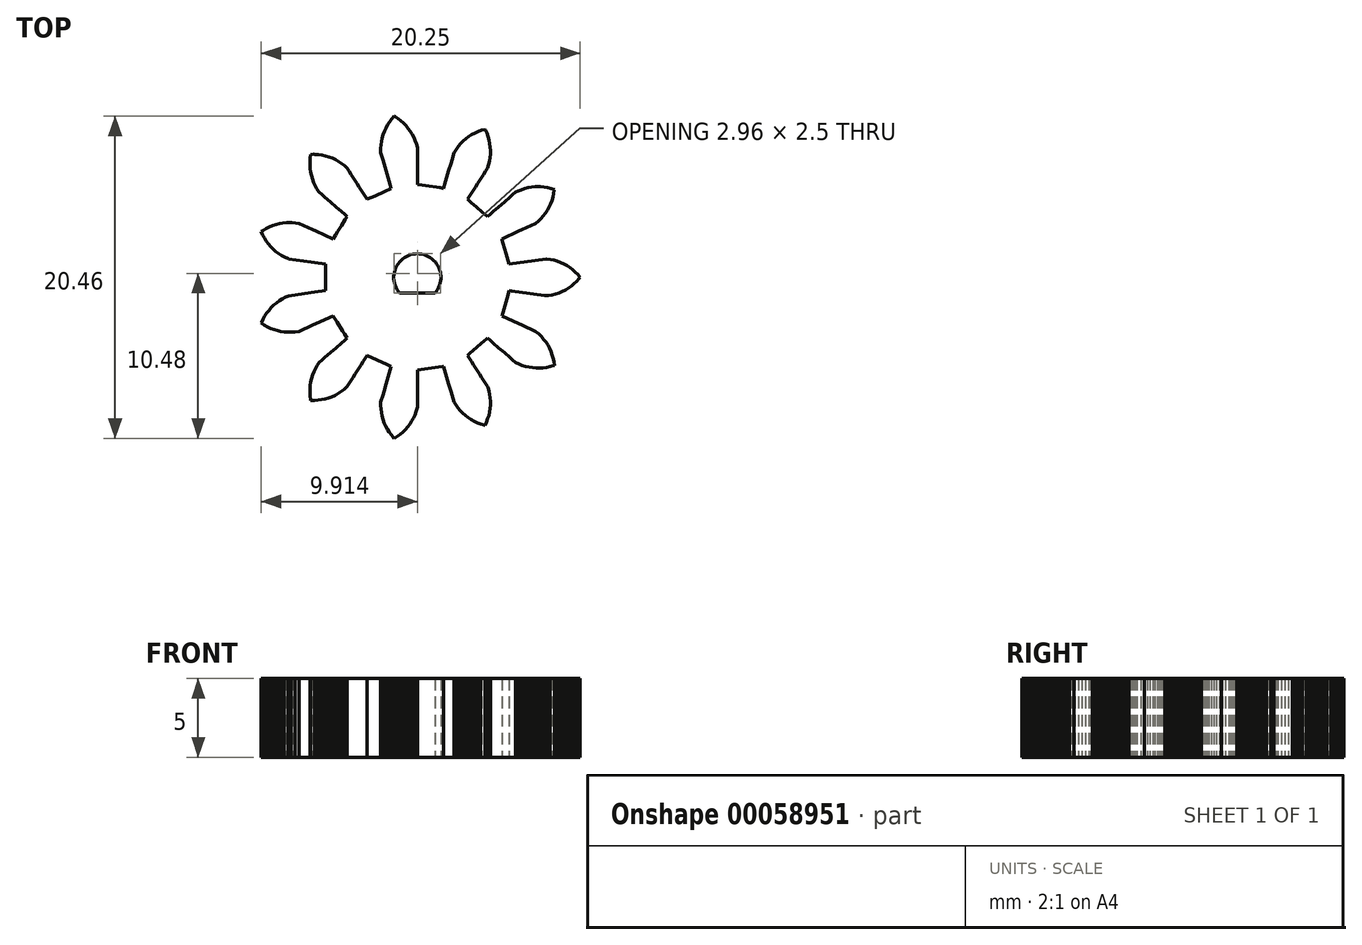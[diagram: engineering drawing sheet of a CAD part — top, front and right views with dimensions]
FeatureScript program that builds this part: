
annotation { "Feature Type Name" : "Feature", "Feature Type Description" : "" }
export const myFeature = defineFeature(function(context is Context, id is Id, definition is map)
    precondition{}
    {
        {
            var Q0;
            Q0=qCreatedBy(makeId("Top.planeOp"),FACE);
            var sketch = newSketch(context, id + "F0", { "sketchPlane" : qUnion([Q0])});
            skLineSegment(sketch, "E0", {"start": v(4.2, -0.84) * mm, "end": v(4.36, -0.86) * mm});
            skLineSegment(sketch, "E1", {"start": v(4.36, -0.86) * mm, "end": v(4.6, -0.9) * mm});
            skLineSegment(sketch, "E2", {"start": v(4.6, -0.9) * mm, "end": v(4.83, -0.93) * mm});
            skLineSegment(sketch, "E3", {"start": v(4.83, -0.93) * mm, "end": v(5.06, -0.96) * mm});
            skLineSegment(sketch, "E4", {"start": v(5.06, -0.96) * mm, "end": v(5.3, -1) * mm});
            skLineSegment(sketch, "E5", {"start": v(5.3, -1) * mm, "end": v(5.53, -1.03) * mm});
            skLineSegment(sketch, "E6", {"start": v(5.53, -1.03) * mm, "end": v(5.76, -1.06) * mm});
            skLineSegment(sketch, "E7", {"start": v(5.76, -1.06) * mm, "end": v(6, -1.1) * mm});
            skLineSegment(sketch, "E8", {"start": v(6, -1.1) * mm, "end": v(6.23, -1.13) * mm});
            skLineSegment(sketch, "E9", {"start": v(6.23, -1.13) * mm, "end": v(6.46, -1.16) * mm});
            skLineSegment(sketch, "E10", {"start": v(6.46, -1.16) * mm, "end": v(6.7, -1.16) * mm});
            skLineSegment(sketch, "E11", {"start": v(6.7, -1.16) * mm, "end": v(6.93, -1.11) * mm});
            skLineSegment(sketch, "E12", {"start": v(6.93, -1.11) * mm, "end": v(7.16, -1.06) * mm});
            skLineSegment(sketch, "E13", {"start": v(7.16, -1.06) * mm, "end": v(7.36, -0.99) * mm});
            skLineSegment(sketch, "E14", {"start": v(7.36, -0.99) * mm, "end": v(7.57, -0.9) * mm});
            skLineSegment(sketch, "E15", {"start": v(7.57, -0.9) * mm, "end": v(7.78, -0.8) * mm});
            skLineSegment(sketch, "E16", {"start": v(7.78, -0.8) * mm, "end": v(7.97, -0.68) * mm});
            skLineSegment(sketch, "E17", {"start": v(7.97, -0.68) * mm, "end": v(8.15, -0.55) * mm});
            skLineSegment(sketch, "E18", {"start": v(8.15, -0.55) * mm, "end": v(8.33, -0.4) * mm});
            skLineSegment(sketch, "E19", {"start": v(8.33, -0.4) * mm, "end": v(8.49, -0.26) * mm});
            skLineSegment(sketch, "E20", {"start": v(8.49, -0.26) * mm, "end": v(8.64, -0.08) * mm});
            skLineSegment(sketch, "E21", {"start": v(8.64, -0.08) * mm, "end": v(8.7, 0) * mm});
            skLineSegment(sketch, "E22", {"start": v(8.7, 0) * mm, "end": v(8.56, 0.17) * mm});
            skLineSegment(sketch, "E23", {"start": v(8.56, 0.17) * mm, "end": v(8.4, 0.34) * mm});
            skLineSegment(sketch, "E24", {"start": v(8.4, 0.34) * mm, "end": v(8.24, 0.48) * mm});
            skLineSegment(sketch, "E25", {"start": v(8.24, 0.48) * mm, "end": v(8.06, 0.62) * mm});
            skLineSegment(sketch, "E26", {"start": v(8.06, 0.62) * mm, "end": v(7.86, 0.75) * mm});
            skLineSegment(sketch, "E27", {"start": v(7.86, 0.75) * mm, "end": v(7.67, 0.85) * mm});
            skLineSegment(sketch, "E28", {"start": v(7.67, 0.85) * mm, "end": v(7.46, 0.95) * mm});
            skLineSegment(sketch, "E29", {"start": v(7.46, 0.95) * mm, "end": v(7.25, 1.03) * mm});
            skLineSegment(sketch, "E30", {"start": v(7.25, 1.03) * mm, "end": v(7.04, 1.1) * mm});
            skLineSegment(sketch, "E31", {"start": v(7.04, 1.1) * mm, "end": v(6.82, 1.14) * mm});
            skLineSegment(sketch, "E32", {"start": v(6.82, 1.14) * mm, "end": v(6.59, 1.17) * mm});
            skLineSegment(sketch, "E33", {"start": v(6.59, 1.17) * mm, "end": v(6.54, 1.17) * mm});
            skLineSegment(sketch, "E34", {"start": v(6.54, 1.17) * mm, "end": v(6.3, 1.14) * mm});
            skLineSegment(sketch, "E35", {"start": v(6.3, 1.14) * mm, "end": v(6.07, 1.1) * mm});
            skLineSegment(sketch, "E36", {"start": v(6.07, 1.1) * mm, "end": v(5.84, 1.07) * mm});
            skLineSegment(sketch, "E37", {"start": v(5.84, 1.07) * mm, "end": v(5.6, 1.04) * mm});
            skLineSegment(sketch, "E38", {"start": v(5.6, 1.04) * mm, "end": v(5.37, 1) * mm});
            skLineSegment(sketch, "E39", {"start": v(5.37, 1) * mm, "end": v(5.14, 0.97) * mm});
            skLineSegment(sketch, "E40", {"start": v(5.14, 0.97) * mm, "end": v(4.9, 0.94) * mm});
            skLineSegment(sketch, "E41", {"start": v(4.9, 0.94) * mm, "end": v(4.67, 0.9) * mm});
            skLineSegment(sketch, "E42", {"start": v(4.67, 0.9) * mm, "end": v(4.44, 0.87) * mm});
            skLineSegment(sketch, "E43", {"start": v(4.44, 0.87) * mm, "end": v(4.2, 0.84) * mm});
            skLineSegment(sketch, "E44", {"start": v(4.2, 0.84) * mm, "end": v(4.14, 1.06) * mm});
            skLineSegment(sketch, "E45", {"start": v(4.14, 1.06) * mm, "end": v(4.08, 1.28) * mm});
            skLineSegment(sketch, "E46", {"start": v(4.08, 1.28) * mm, "end": v(4.01, 1.5) * mm});
            skLineSegment(sketch, "E47", {"start": v(4.01, 1.5) * mm, "end": v(3.95, 1.72) * mm});
            skLineSegment(sketch, "E48", {"start": v(3.95, 1.72) * mm, "end": v(3.88, 1.94) * mm});
            skLineSegment(sketch, "E49", {"start": v(3.88, 1.94) * mm, "end": v(3.82, 2.16) * mm});
            skLineSegment(sketch, "E50", {"start": v(3.82, 2.16) * mm, "end": v(3.76, 2.38) * mm});
            skLineSegment(sketch, "E51", {"start": v(3.76, 2.38) * mm, "end": v(3.74, 2.45) * mm});
            skLineSegment(sketch, "E52", {"start": v(3.74, 2.45) * mm, "end": v(3.95, 2.55) * mm});
            skLineSegment(sketch, "E53", {"start": v(3.95, 2.55) * mm, "end": v(4.16, 2.64) * mm});
            skLineSegment(sketch, "E54", {"start": v(4.16, 2.64) * mm, "end": v(4.38, 2.74) * mm});
            skLineSegment(sketch, "E55", {"start": v(4.38, 2.74) * mm, "end": v(4.6, 2.84) * mm});
            skLineSegment(sketch, "E56", {"start": v(4.6, 2.84) * mm, "end": v(4.8, 2.94) * mm});
            skLineSegment(sketch, "E57", {"start": v(4.8, 2.94) * mm, "end": v(5.02, 3.04) * mm});
            skLineSegment(sketch, "E58", {"start": v(5.02, 3.04) * mm, "end": v(5.24, 3.13) * mm});
            skLineSegment(sketch, "E59", {"start": v(5.24, 3.13) * mm, "end": v(5.45, 3.23) * mm});
            skLineSegment(sketch, "E60", {"start": v(5.45, 3.23) * mm, "end": v(5.66, 3.33) * mm});
            skLineSegment(sketch, "E61", {"start": v(5.66, 3.33) * mm, "end": v(5.88, 3.43) * mm});
            skLineSegment(sketch, "E62", {"start": v(5.88, 3.43) * mm, "end": v(6.05, 3.57) * mm});
            skLineSegment(sketch, "E63", {"start": v(6.05, 3.57) * mm, "end": v(6.22, 3.73) * mm});
            skLineSegment(sketch, "E64", {"start": v(6.22, 3.73) * mm, "end": v(6.37, 3.9) * mm});
            skLineSegment(sketch, "E65", {"start": v(6.37, 3.9) * mm, "end": v(6.5, 4.08) * mm});
            skLineSegment(sketch, "E66", {"start": v(6.5, 4.08) * mm, "end": v(6.63, 4.27) * mm});
            skLineSegment(sketch, "E67", {"start": v(6.63, 4.27) * mm, "end": v(6.74, 4.46) * mm});
            skLineSegment(sketch, "E68", {"start": v(6.74, 4.46) * mm, "end": v(6.84, 4.67) * mm});
            skLineSegment(sketch, "E69", {"start": v(6.84, 4.67) * mm, "end": v(6.92, 4.88) * mm});
            skLineSegment(sketch, "E70", {"start": v(6.92, 4.88) * mm, "end": v(6.98, 5.09) * mm});
            skLineSegment(sketch, "E71", {"start": v(6.98, 5.09) * mm, "end": v(7.03, 5.31) * mm});
            skLineSegment(sketch, "E72", {"start": v(7.03, 5.31) * mm, "end": v(7.06, 5.54) * mm});
            skLineSegment(sketch, "E73", {"start": v(7.06, 5.54) * mm, "end": v(7.07, 5.59) * mm});
            skLineSegment(sketch, "E74", {"start": v(7.07, 5.59) * mm, "end": v(6.85, 5.65) * mm});
            skLineSegment(sketch, "E75", {"start": v(6.85, 5.65) * mm, "end": v(6.63, 5.7) * mm});
            skLineSegment(sketch, "E76", {"start": v(6.63, 5.7) * mm, "end": v(6.41, 5.74) * mm});
            skLineSegment(sketch, "E77", {"start": v(6.41, 5.74) * mm, "end": v(6.18, 5.76) * mm});
            skLineSegment(sketch, "E78", {"start": v(6.18, 5.76) * mm, "end": v(6.07, 5.76) * mm});
            skLineSegment(sketch, "E79", {"start": v(6.07, 5.76) * mm, "end": v(5.84, 5.75) * mm});
            skLineSegment(sketch, "E80", {"start": v(5.84, 5.75) * mm, "end": v(5.62, 5.73) * mm});
            skLineSegment(sketch, "E81", {"start": v(5.62, 5.73) * mm, "end": v(5.4, 5.7) * mm});
            skLineSegment(sketch, "E82", {"start": v(5.4, 5.7) * mm, "end": v(5.18, 5.63) * mm});
            skLineSegment(sketch, "E83", {"start": v(5.18, 5.63) * mm, "end": v(4.96, 5.56) * mm});
            skLineSegment(sketch, "E84", {"start": v(4.96, 5.56) * mm, "end": v(4.76, 5.48) * mm});
            skLineSegment(sketch, "E85", {"start": v(4.76, 5.48) * mm, "end": v(4.6, 5.4) * mm});
            skLineSegment(sketch, "E86", {"start": v(4.6, 5.4) * mm, "end": v(4.43, 5.25) * mm});
            skLineSegment(sketch, "E87", {"start": v(4.43, 5.25) * mm, "end": v(4.25, 5.1) * mm});
            skLineSegment(sketch, "E88", {"start": v(4.25, 5.1) * mm, "end": v(4.07, 4.94) * mm});
            skLineSegment(sketch, "E89", {"start": v(4.07, 4.94) * mm, "end": v(3.9, 4.79) * mm});
            skLineSegment(sketch, "E90", {"start": v(3.9, 4.79) * mm, "end": v(3.72, 4.63) * mm});
            skLineSegment(sketch, "E91", {"start": v(3.72, 4.63) * mm, "end": v(3.54, 4.48) * mm});
            skLineSegment(sketch, "E92", {"start": v(3.54, 4.48) * mm, "end": v(3.36, 4.32) * mm});
            skLineSegment(sketch, "E93", {"start": v(3.36, 4.32) * mm, "end": v(3.18, 4.17) * mm});
            skLineSegment(sketch, "E94", {"start": v(3.18, 4.17) * mm, "end": v(3, 4.01) * mm});
            skLineSegment(sketch, "E95", {"start": v(3, 4.01) * mm, "end": v(2.83, 3.86) * mm});
            skLineSegment(sketch, "E96", {"start": v(2.83, 3.86) * mm, "end": v(2.65, 4) * mm});
            skLineSegment(sketch, "E97", {"start": v(2.65, 4) * mm, "end": v(2.48, 4.16) * mm});
            skLineSegment(sketch, "E98", {"start": v(2.48, 4.16) * mm, "end": v(2.3, 4.31) * mm});
            skLineSegment(sketch, "E99", {"start": v(2.3, 4.31) * mm, "end": v(2.13, 4.46) * mm});
            skLineSegment(sketch, "E100", {"start": v(2.13, 4.46) * mm, "end": v(1.96, 4.61) * mm});
            skLineSegment(sketch, "E101", {"start": v(1.96, 4.61) * mm, "end": v(1.79, 4.76) * mm});
            skLineSegment(sketch, "E102", {"start": v(1.79, 4.76) * mm, "end": v(1.62, 4.91) * mm});
            skLineSegment(sketch, "E103", {"start": v(1.62, 4.91) * mm, "end": v(1.56, 4.96) * mm});
            skLineSegment(sketch, "E104", {"start": v(1.56, 4.96) * mm, "end": v(1.69, 5.16) * mm});
            skLineSegment(sketch, "E105", {"start": v(1.69, 5.16) * mm, "end": v(1.82, 5.35) * mm});
            skLineSegment(sketch, "E106", {"start": v(1.82, 5.35) * mm, "end": v(1.94, 5.55) * mm});
            skLineSegment(sketch, "E107", {"start": v(1.94, 5.55) * mm, "end": v(2.07, 5.75) * mm});
            skLineSegment(sketch, "E108", {"start": v(2.07, 5.75) * mm, "end": v(2.2, 5.95) * mm});
            skLineSegment(sketch, "E109", {"start": v(2.2, 5.95) * mm, "end": v(2.32, 6.15) * mm});
            skLineSegment(sketch, "E110", {"start": v(2.32, 6.15) * mm, "end": v(2.45, 6.35) * mm});
            skLineSegment(sketch, "E111", {"start": v(2.45, 6.35) * mm, "end": v(2.58, 6.54) * mm});
            skLineSegment(sketch, "E112", {"start": v(2.58, 6.54) * mm, "end": v(2.7, 6.74) * mm});
            skLineSegment(sketch, "E113", {"start": v(2.7, 6.74) * mm, "end": v(2.83, 6.94) * mm});
            skLineSegment(sketch, "E114", {"start": v(2.83, 6.94) * mm, "end": v(2.9, 7.16) * mm});
            skLineSegment(sketch, "E115", {"start": v(2.9, 7.16) * mm, "end": v(2.95, 7.38) * mm});
            skLineSegment(sketch, "E116", {"start": v(2.95, 7.38) * mm, "end": v(3, 7.6) * mm});
            skLineSegment(sketch, "E117", {"start": v(3, 7.6) * mm, "end": v(3.01, 7.83) * mm});
            skLineSegment(sketch, "E118", {"start": v(3.01, 7.83) * mm, "end": v(3.01, 8.06) * mm});
            skLineSegment(sketch, "E119", {"start": v(3.01, 8.06) * mm, "end": v(3, 8.27) * mm});
            skLineSegment(sketch, "E120", {"start": v(3, 8.27) * mm, "end": v(2.97, 8.5) * mm});
            skLineSegment(sketch, "E121", {"start": v(2.97, 8.5) * mm, "end": v(2.92, 8.72) * mm});
            skLineSegment(sketch, "E122", {"start": v(2.92, 8.72) * mm, "end": v(2.86, 8.93) * mm});
            skLineSegment(sketch, "E123", {"start": v(2.86, 8.93) * mm, "end": v(2.78, 9.15) * mm});
            skLineSegment(sketch, "E124", {"start": v(2.78, 9.15) * mm, "end": v(2.69, 9.36) * mm});
            skLineSegment(sketch, "E125", {"start": v(2.69, 9.36) * mm, "end": v(2.67, 9.4) * mm});
            skLineSegment(sketch, "E126", {"start": v(2.67, 9.4) * mm, "end": v(2.45, 9.34) * mm});
            skLineSegment(sketch, "E127", {"start": v(2.45, 9.34) * mm, "end": v(2.23, 9.26) * mm});
            skLineSegment(sketch, "E128", {"start": v(2.23, 9.26) * mm, "end": v(2.03, 9.17) * mm});
            skLineSegment(sketch, "E129", {"start": v(2.03, 9.17) * mm, "end": v(1.83, 9.06) * mm});
            skLineSegment(sketch, "E130", {"start": v(1.83, 9.06) * mm, "end": v(1.64, 8.94) * mm});
            skLineSegment(sketch, "E131", {"start": v(1.64, 8.94) * mm, "end": v(1.46, 8.81) * mm});
            skLineSegment(sketch, "E132", {"start": v(1.46, 8.81) * mm, "end": v(1.29, 8.66) * mm});
            skLineSegment(sketch, "E133", {"start": v(1.29, 8.66) * mm, "end": v(1.13, 8.5) * mm});
            skLineSegment(sketch, "E134", {"start": v(1.13, 8.5) * mm, "end": v(0.98, 8.34) * mm});
            skLineSegment(sketch, "E135", {"start": v(0.98, 8.34) * mm, "end": v(0.85, 8.15) * mm});
            skLineSegment(sketch, "E136", {"start": v(0.85, 8.15) * mm, "end": v(0.72, 7.96) * mm});
            skLineSegment(sketch, "E137", {"start": v(0.72, 7.96) * mm, "end": v(0.7, 7.92) * mm});
            skLineSegment(sketch, "E138", {"start": v(0.7, 7.92) * mm, "end": v(0.63, 7.69) * mm});
            skLineSegment(sketch, "E139", {"start": v(0.63, 7.69) * mm, "end": v(0.57, 7.46) * mm});
            skLineSegment(sketch, "E140", {"start": v(0.57, 7.46) * mm, "end": v(0.5, 7.24) * mm});
            skLineSegment(sketch, "E141", {"start": v(0.5, 7.24) * mm, "end": v(0.43, 7.01) * mm});
            skLineSegment(sketch, "E142", {"start": v(0.43, 7.01) * mm, "end": v(0.37, 6.79) * mm});
            skLineSegment(sketch, "E143", {"start": v(0.37, 6.79) * mm, "end": v(0.3, 6.56) * mm});
            skLineSegment(sketch, "E144", {"start": v(0.3, 6.56) * mm, "end": v(0.23, 6.33) * mm});
            skLineSegment(sketch, "E145", {"start": v(0.23, 6.33) * mm, "end": v(0.17, 6.1) * mm});
            skLineSegment(sketch, "E146", {"start": v(0.17, 6.1) * mm, "end": v(0.1, 5.88) * mm});
            skLineSegment(sketch, "E147", {"start": v(0.1, 5.88) * mm, "end": v(0.03, 5.66) * mm});
            skLineSegment(sketch, "E148", {"start": v(0.03, 5.66) * mm, "end": v(-0.2, 5.69) * mm});
            skLineSegment(sketch, "E149", {"start": v(-0.2, 5.69) * mm, "end": v(-0.42, 5.72) * mm});
            skLineSegment(sketch, "E150", {"start": v(-0.42, 5.72) * mm, "end": v(-0.65, 5.75) * mm});
            skLineSegment(sketch, "E151", {"start": v(-0.65, 5.75) * mm, "end": v(-0.87, 5.79) * mm});
            skLineSegment(sketch, "E152", {"start": v(-0.87, 5.79) * mm, "end": v(-1.1, 5.82) * mm});
            skLineSegment(sketch, "E153", {"start": v(-1.1, 5.82) * mm, "end": v(-1.33, 5.85) * mm});
            skLineSegment(sketch, "E154", {"start": v(-1.33, 5.85) * mm, "end": v(-1.55, 5.88) * mm});
            skLineSegment(sketch, "E155", {"start": v(-1.55, 5.88) * mm, "end": v(-1.63, 5.9) * mm});
            skLineSegment(sketch, "E156", {"start": v(-1.63, 5.9) * mm, "end": v(-1.63, 6.13) * mm});
            skLineSegment(sketch, "E157", {"start": v(-1.63, 6.13) * mm, "end": v(-1.63, 6.37) * mm});
            skLineSegment(sketch, "E158", {"start": v(-1.63, 6.37) * mm, "end": v(-1.63, 6.6) * mm});
            skLineSegment(sketch, "E159", {"start": v(-1.63, 6.6) * mm, "end": v(-1.63, 6.84) * mm});
            skLineSegment(sketch, "E160", {"start": v(-1.63, 6.84) * mm, "end": v(-1.63, 7.07) * mm});
            skLineSegment(sketch, "E161", {"start": v(-1.63, 7.07) * mm, "end": v(-1.63, 7.3) * mm});
            skLineSegment(sketch, "E162", {"start": v(-1.63, 7.3) * mm, "end": v(-1.63, 7.54) * mm});
            skLineSegment(sketch, "E163", {"start": v(-1.63, 7.54) * mm, "end": v(-1.63, 7.78) * mm});
            skLineSegment(sketch, "E164", {"start": v(-1.63, 7.78) * mm, "end": v(-1.63, 8.01) * mm});
            skLineSegment(sketch, "E165", {"start": v(-1.63, 8.01) * mm, "end": v(-1.63, 8.25) * mm});
            skLineSegment(sketch, "E166", {"start": v(-1.63, 8.25) * mm, "end": v(-1.69, 8.47) * mm});
            skLineSegment(sketch, "E167", {"start": v(-1.69, 8.47) * mm, "end": v(-1.76, 8.69) * mm});
            skLineSegment(sketch, "E168", {"start": v(-1.76, 8.69) * mm, "end": v(-1.85, 8.89) * mm});
            skLineSegment(sketch, "E169", {"start": v(-1.85, 8.89) * mm, "end": v(-1.96, 9.1) * mm});
            skLineSegment(sketch, "E170", {"start": v(-1.96, 9.1) * mm, "end": v(-2.08, 9.28) * mm});
            skLineSegment(sketch, "E171", {"start": v(-2.08, 9.28) * mm, "end": v(-2.2, 9.46) * mm});
            skLineSegment(sketch, "E172", {"start": v(-2.2, 9.46) * mm, "end": v(-2.35, 9.64) * mm});
            skLineSegment(sketch, "E173", {"start": v(-2.35, 9.64) * mm, "end": v(-2.52, 9.8) * mm});
            skLineSegment(sketch, "E174", {"start": v(-2.52, 9.8) * mm, "end": v(-2.68, 9.94) * mm});
            skLineSegment(sketch, "E175", {"start": v(-2.68, 9.94) * mm, "end": v(-2.86, 10.08) * mm});
            skLineSegment(sketch, "E176", {"start": v(-2.86, 10.08) * mm, "end": v(-3.06, 10.2) * mm});
            skLineSegment(sketch, "E177", {"start": v(-3.06, 10.2) * mm, "end": v(-3.1, 10.23) * mm});
            skLineSegment(sketch, "E178", {"start": v(-3.1, 10.23) * mm, "end": v(-3.25, 10.06) * mm});
            skLineSegment(sketch, "E179", {"start": v(-3.25, 10.06) * mm, "end": v(-3.39, 9.88) * mm});
            skLineSegment(sketch, "E180", {"start": v(-3.39, 9.88) * mm, "end": v(-3.5, 9.7) * mm});
            skLineSegment(sketch, "E181", {"start": v(-3.5, 9.7) * mm, "end": v(-3.62, 9.5) * mm});
            skLineSegment(sketch, "E182", {"start": v(-3.62, 9.5) * mm, "end": v(-3.72, 9.29) * mm});
            skLineSegment(sketch, "E183", {"start": v(-3.72, 9.29) * mm, "end": v(-3.8, 9.08) * mm});
            skLineSegment(sketch, "E184", {"start": v(-3.8, 9.08) * mm, "end": v(-3.86, 8.86) * mm});
            skLineSegment(sketch, "E185", {"start": v(-3.86, 8.86) * mm, "end": v(-3.9, 8.64) * mm});
            skLineSegment(sketch, "E186", {"start": v(-3.9, 8.64) * mm, "end": v(-3.94, 8.42) * mm});
            skLineSegment(sketch, "E187", {"start": v(-3.94, 8.42) * mm, "end": v(-3.95, 8.2) * mm});
            skLineSegment(sketch, "E188", {"start": v(-3.95, 8.2) * mm, "end": v(-3.95, 7.96) * mm});
            skLineSegment(sketch, "E189", {"start": v(-3.95, 7.96) * mm, "end": v(-3.95, 7.92) * mm});
            skLineSegment(sketch, "E190", {"start": v(-3.95, 7.92) * mm, "end": v(-3.88, 7.69) * mm});
            skLineSegment(sketch, "E191", {"start": v(-3.88, 7.69) * mm, "end": v(-3.82, 7.46) * mm});
            skLineSegment(sketch, "E192", {"start": v(-3.82, 7.46) * mm, "end": v(-3.75, 7.24) * mm});
            skLineSegment(sketch, "E193", {"start": v(-3.75, 7.24) * mm, "end": v(-3.68, 7.01) * mm});
            skLineSegment(sketch, "E194", {"start": v(-3.68, 7.01) * mm, "end": v(-3.62, 6.79) * mm});
            skLineSegment(sketch, "E195", {"start": v(-3.62, 6.79) * mm, "end": v(-3.55, 6.56) * mm});
            skLineSegment(sketch, "E196", {"start": v(-3.55, 6.56) * mm, "end": v(-3.49, 6.33) * mm});
            skLineSegment(sketch, "E197", {"start": v(-3.49, 6.33) * mm, "end": v(-3.42, 6.1) * mm});
            skLineSegment(sketch, "E198", {"start": v(-3.42, 6.1) * mm, "end": v(-3.35, 5.88) * mm});
            skLineSegment(sketch, "E199", {"start": v(-3.35, 5.88) * mm, "end": v(-3.29, 5.66) * mm});
            skLineSegment(sketch, "E200", {"start": v(-3.29, 5.66) * mm, "end": v(-3.5, 5.56) * mm});
            skLineSegment(sketch, "E201", {"start": v(-3.5, 5.56) * mm, "end": v(-3.7, 5.46) * mm});
            skLineSegment(sketch, "E202", {"start": v(-3.7, 5.46) * mm, "end": v(-3.91, 5.37) * mm});
            skLineSegment(sketch, "E203", {"start": v(-3.91, 5.37) * mm, "end": v(-4.12, 5.27) * mm});
            skLineSegment(sketch, "E204", {"start": v(-4.12, 5.27) * mm, "end": v(-4.33, 5.18) * mm});
            skLineSegment(sketch, "E205", {"start": v(-4.33, 5.18) * mm, "end": v(-4.54, 5.08) * mm});
            skLineSegment(sketch, "E206", {"start": v(-4.54, 5.08) * mm, "end": v(-4.75, 4.99) * mm});
            skLineSegment(sketch, "E207", {"start": v(-4.75, 4.99) * mm, "end": v(-4.81, 4.96) * mm});
            skLineSegment(sketch, "E208", {"start": v(-4.81, 4.96) * mm, "end": v(-4.94, 5.16) * mm});
            skLineSegment(sketch, "E209", {"start": v(-4.94, 5.16) * mm, "end": v(-5.07, 5.35) * mm});
            skLineSegment(sketch, "E210", {"start": v(-5.07, 5.35) * mm, "end": v(-5.2, 5.55) * mm});
            skLineSegment(sketch, "E211", {"start": v(-5.2, 5.55) * mm, "end": v(-5.32, 5.75) * mm});
            skLineSegment(sketch, "E212", {"start": v(-5.32, 5.75) * mm, "end": v(-5.45, 5.95) * mm});
            skLineSegment(sketch, "E213", {"start": v(-5.45, 5.95) * mm, "end": v(-5.58, 6.15) * mm});
            skLineSegment(sketch, "E214", {"start": v(-5.58, 6.15) * mm, "end": v(-5.7, 6.35) * mm});
            skLineSegment(sketch, "E215", {"start": v(-5.7, 6.35) * mm, "end": v(-5.83, 6.54) * mm});
            skLineSegment(sketch, "E216", {"start": v(-5.83, 6.54) * mm, "end": v(-5.96, 6.74) * mm});
            skLineSegment(sketch, "E217", {"start": v(-5.96, 6.74) * mm, "end": v(-6.09, 6.94) * mm});
            skLineSegment(sketch, "E218", {"start": v(-6.09, 6.94) * mm, "end": v(-6.26, 7.1) * mm});
            skLineSegment(sketch, "E219", {"start": v(-6.26, 7.1) * mm, "end": v(-6.44, 7.23) * mm});
            skLineSegment(sketch, "E220", {"start": v(-6.44, 7.23) * mm, "end": v(-6.62, 7.36) * mm});
            skLineSegment(sketch, "E221", {"start": v(-6.62, 7.36) * mm, "end": v(-6.82, 7.47) * mm});
            skLineSegment(sketch, "E222", {"start": v(-6.82, 7.47) * mm, "end": v(-7.03, 7.57) * mm});
            skLineSegment(sketch, "E223", {"start": v(-7.03, 7.57) * mm, "end": v(-7.23, 7.65) * mm});
            skLineSegment(sketch, "E224", {"start": v(-7.23, 7.65) * mm, "end": v(-7.45, 7.71) * mm});
            skLineSegment(sketch, "E225", {"start": v(-7.45, 7.71) * mm, "end": v(-7.67, 7.76) * mm});
            skLineSegment(sketch, "E226", {"start": v(-7.67, 7.76) * mm, "end": v(-7.89, 7.8) * mm});
            skLineSegment(sketch, "E227", {"start": v(-7.89, 7.8) * mm, "end": v(-8.12, 7.81) * mm});
            skLineSegment(sketch, "E228", {"start": v(-8.12, 7.81) * mm, "end": v(-8.23, 7.81) * mm});
            skLineSegment(sketch, "E229", {"start": v(-8.23, 7.81) * mm, "end": v(-8.4, 7.81) * mm});
            skLineSegment(sketch, "E230", {"start": v(-8.4, 7.81) * mm, "end": v(-8.43, 7.58) * mm});
            skLineSegment(sketch, "E231", {"start": v(-8.43, 7.58) * mm, "end": v(-8.45, 7.36) * mm});
            skLineSegment(sketch, "E232", {"start": v(-8.45, 7.36) * mm, "end": v(-8.45, 7.14) * mm});
            skLineSegment(sketch, "E233", {"start": v(-8.45, 7.14) * mm, "end": v(-8.44, 6.9) * mm});
            skLineSegment(sketch, "E234", {"start": v(-8.44, 6.9) * mm, "end": v(-8.4, 6.68) * mm});
            skLineSegment(sketch, "E235", {"start": v(-8.4, 6.68) * mm, "end": v(-8.36, 6.47) * mm});
            skLineSegment(sketch, "E236", {"start": v(-8.36, 6.47) * mm, "end": v(-8.3, 6.25) * mm});
            skLineSegment(sketch, "E237", {"start": v(-8.3, 6.25) * mm, "end": v(-8.21, 6.03) * mm});
            skLineSegment(sketch, "E238", {"start": v(-8.21, 6.03) * mm, "end": v(-8.13, 5.84) * mm});
            skLineSegment(sketch, "E239", {"start": v(-8.13, 5.84) * mm, "end": v(-8.01, 5.63) * mm});
            skLineSegment(sketch, "E240", {"start": v(-8.01, 5.63) * mm, "end": v(-7.89, 5.44) * mm});
            skLineSegment(sketch, "E241", {"start": v(-7.89, 5.44) * mm, "end": v(-7.86, 5.4) * mm});
            skLineSegment(sketch, "E242", {"start": v(-7.86, 5.4) * mm, "end": v(-7.68, 5.25) * mm});
            skLineSegment(sketch, "E243", {"start": v(-7.68, 5.25) * mm, "end": v(-7.5, 5.1) * mm});
            skLineSegment(sketch, "E244", {"start": v(-7.5, 5.1) * mm, "end": v(-7.33, 4.94) * mm});
            skLineSegment(sketch, "E245", {"start": v(-7.33, 4.94) * mm, "end": v(-7.15, 4.79) * mm});
            skLineSegment(sketch, "E246", {"start": v(-7.15, 4.79) * mm, "end": v(-6.97, 4.63) * mm});
            skLineSegment(sketch, "E247", {"start": v(-6.97, 4.63) * mm, "end": v(-6.8, 4.48) * mm});
            skLineSegment(sketch, "E248", {"start": v(-6.8, 4.48) * mm, "end": v(-6.61, 4.32) * mm});
            skLineSegment(sketch, "E249", {"start": v(-6.61, 4.32) * mm, "end": v(-6.44, 4.17) * mm});
            skLineSegment(sketch, "E250", {"start": v(-6.44, 4.17) * mm, "end": v(-6.26, 4.01) * mm});
            skLineSegment(sketch, "E251", {"start": v(-6.26, 4.01) * mm, "end": v(-6.08, 3.86) * mm});
            skLineSegment(sketch, "E252", {"start": v(-6.08, 3.86) * mm, "end": v(-6.2, 3.67) * mm});
            skLineSegment(sketch, "E253", {"start": v(-6.2, 3.67) * mm, "end": v(-6.33, 3.47) * mm});
            skLineSegment(sketch, "E254", {"start": v(-6.33, 3.47) * mm, "end": v(-6.45, 3.28) * mm});
            skLineSegment(sketch, "E255", {"start": v(-6.45, 3.28) * mm, "end": v(-6.58, 3.09) * mm});
            skLineSegment(sketch, "E256", {"start": v(-6.58, 3.09) * mm, "end": v(-6.7, 2.9) * mm});
            skLineSegment(sketch, "E257", {"start": v(-6.7, 2.9) * mm, "end": v(-6.82, 2.7) * mm});
            skLineSegment(sketch, "E258", {"start": v(-6.82, 2.7) * mm, "end": v(-6.95, 2.5) * mm});
            skLineSegment(sketch, "E259", {"start": v(-6.95, 2.5) * mm, "end": v(-6.99, 2.45) * mm});
            skLineSegment(sketch, "E260", {"start": v(-6.99, 2.45) * mm, "end": v(-7.2, 2.55) * mm});
            skLineSegment(sketch, "E261", {"start": v(-7.2, 2.55) * mm, "end": v(-7.42, 2.64) * mm});
            skLineSegment(sketch, "E262", {"start": v(-7.42, 2.64) * mm, "end": v(-7.63, 2.74) * mm});
            skLineSegment(sketch, "E263", {"start": v(-7.63, 2.74) * mm, "end": v(-7.84, 2.84) * mm});
            skLineSegment(sketch, "E264", {"start": v(-7.84, 2.84) * mm, "end": v(-8.06, 2.94) * mm});
            skLineSegment(sketch, "E265", {"start": v(-8.06, 2.94) * mm, "end": v(-8.27, 3.04) * mm});
            skLineSegment(sketch, "E266", {"start": v(-8.27, 3.04) * mm, "end": v(-8.49, 3.13) * mm});
            skLineSegment(sketch, "E267", {"start": v(-8.49, 3.13) * mm, "end": v(-8.7, 3.23) * mm});
            skLineSegment(sketch, "E268", {"start": v(-8.7, 3.23) * mm, "end": v(-8.92, 3.33) * mm});
            skLineSegment(sketch, "E269", {"start": v(-8.92, 3.33) * mm, "end": v(-9.13, 3.43) * mm});
            skLineSegment(sketch, "E270", {"start": v(-9.13, 3.43) * mm, "end": v(-9.36, 3.46) * mm});
            skLineSegment(sketch, "E271", {"start": v(-9.36, 3.46) * mm, "end": v(-9.59, 3.48) * mm});
            skLineSegment(sketch, "E272", {"start": v(-9.59, 3.48) * mm, "end": v(-9.72, 3.49) * mm});
            skLineSegment(sketch, "E273", {"start": v(-9.72, 3.49) * mm, "end": v(-9.95, 3.48) * mm});
            skLineSegment(sketch, "E274", {"start": v(-9.95, 3.48) * mm, "end": v(-10.18, 3.46) * mm});
            skLineSegment(sketch, "E275", {"start": v(-10.18, 3.46) * mm, "end": v(-10.4, 3.42) * mm});
            skLineSegment(sketch, "E276", {"start": v(-10.4, 3.42) * mm, "end": v(-10.61, 3.36) * mm});
            skLineSegment(sketch, "E277", {"start": v(-10.61, 3.36) * mm, "end": v(-10.83, 3.3) * mm});
            skLineSegment(sketch, "E278", {"start": v(-10.83, 3.3) * mm, "end": v(-11.03, 3.2) * mm});
            skLineSegment(sketch, "E279", {"start": v(-11.03, 3.2) * mm, "end": v(-11.24, 3.1) * mm});
            skLineSegment(sketch, "E280", {"start": v(-11.24, 3.1) * mm, "end": v(-11.43, 2.99) * mm});
            skLineSegment(sketch, "E281", {"start": v(-11.43, 2.99) * mm, "end": v(-11.54, 2.91) * mm});
            skLineSegment(sketch, "E282", {"start": v(-11.54, 2.91) * mm, "end": v(-11.45, 2.7) * mm});
            skLineSegment(sketch, "E283", {"start": v(-11.45, 2.7) * mm, "end": v(-11.34, 2.5) * mm});
            skLineSegment(sketch, "E284", {"start": v(-11.34, 2.5) * mm, "end": v(-11.23, 2.31) * mm});
            skLineSegment(sketch, "E285", {"start": v(-11.23, 2.31) * mm, "end": v(-11.1, 2.13) * mm});
            skLineSegment(sketch, "E286", {"start": v(-11.1, 2.13) * mm, "end": v(-10.94, 1.96) * mm});
            skLineSegment(sketch, "E287", {"start": v(-10.94, 1.96) * mm, "end": v(-10.79, 1.8) * mm});
            skLineSegment(sketch, "E288", {"start": v(-10.79, 1.8) * mm, "end": v(-10.62, 1.65) * mm});
            skLineSegment(sketch, "E289", {"start": v(-10.62, 1.65) * mm, "end": v(-10.43, 1.51) * mm});
            skLineSegment(sketch, "E290", {"start": v(-10.43, 1.51) * mm, "end": v(-10.25, 1.4) * mm});
            skLineSegment(sketch, "E291", {"start": v(-10.25, 1.4) * mm, "end": v(-10.05, 1.29) * mm});
            skLineSegment(sketch, "E292", {"start": v(-10.05, 1.29) * mm, "end": v(-9.84, 1.2) * mm});
            skLineSegment(sketch, "E293", {"start": v(-9.84, 1.2) * mm, "end": v(-9.8, 1.17) * mm});
            skLineSegment(sketch, "E294", {"start": v(-9.8, 1.17) * mm, "end": v(-9.56, 1.14) * mm});
            skLineSegment(sketch, "E295", {"start": v(-9.56, 1.14) * mm, "end": v(-9.33, 1.1) * mm});
            skLineSegment(sketch, "E296", {"start": v(-9.33, 1.1) * mm, "end": v(-9.1, 1.07) * mm});
            skLineSegment(sketch, "E297", {"start": v(-9.1, 1.07) * mm, "end": v(-8.86, 1.04) * mm});
            skLineSegment(sketch, "E298", {"start": v(-8.86, 1.04) * mm, "end": v(-8.63, 1) * mm});
            skLineSegment(sketch, "E299", {"start": v(-8.63, 1) * mm, "end": v(-8.4, 0.97) * mm});
            skLineSegment(sketch, "E300", {"start": v(-8.4, 0.97) * mm, "end": v(-8.16, 0.94) * mm});
            skLineSegment(sketch, "E301", {"start": v(-8.16, 0.94) * mm, "end": v(-7.93, 0.9) * mm});
            skLineSegment(sketch, "E302", {"start": v(-7.93, 0.9) * mm, "end": v(-7.7, 0.87) * mm});
            skLineSegment(sketch, "E303", {"start": v(-7.7, 0.87) * mm, "end": v(-7.46, 0.84) * mm});
            skLineSegment(sketch, "E304", {"start": v(-7.46, 0.84) * mm, "end": v(-7.46, 0.6) * mm});
            skLineSegment(sketch, "E305", {"start": v(-7.46, 0.6) * mm, "end": v(-7.46, 0.38) * mm});
            skLineSegment(sketch, "E306", {"start": v(-7.46, 0.38) * mm, "end": v(-7.46, 0.15) * mm});
            skLineSegment(sketch, "E307", {"start": v(-7.46, 0.15) * mm, "end": v(-7.46, -0.08) * mm});
            skLineSegment(sketch, "E308", {"start": v(-7.46, -0.08) * mm, "end": v(-7.46, -0.3) * mm});
            skLineSegment(sketch, "E309", {"start": v(-7.46, -0.3) * mm, "end": v(-7.46, -0.54) * mm});
            skLineSegment(sketch, "E310", {"start": v(-7.46, -0.54) * mm, "end": v(-7.46, -0.77) * mm});
            skLineSegment(sketch, "E311", {"start": v(-7.46, -0.77) * mm, "end": v(-7.46, -0.84) * mm});
            skLineSegment(sketch, "E312", {"start": v(-7.46, -0.84) * mm, "end": v(-7.7, -0.87) * mm});
            skLineSegment(sketch, "E313", {"start": v(-7.7, -0.87) * mm, "end": v(-7.93, -0.9) * mm});
            skLineSegment(sketch, "E314", {"start": v(-7.93, -0.9) * mm, "end": v(-8.16, -0.94) * mm});
            skLineSegment(sketch, "E315", {"start": v(-8.16, -0.94) * mm, "end": v(-8.4, -0.97) * mm});
            skLineSegment(sketch, "E316", {"start": v(-8.4, -0.97) * mm, "end": v(-8.63, -1) * mm});
            skLineSegment(sketch, "E317", {"start": v(-8.63, -1) * mm, "end": v(-8.86, -1.04) * mm});
            skLineSegment(sketch, "E318", {"start": v(-8.86, -1.04) * mm, "end": v(-9.1, -1.07) * mm});
            skLineSegment(sketch, "E319", {"start": v(-9.1, -1.07) * mm, "end": v(-9.33, -1.1) * mm});
            skLineSegment(sketch, "E320", {"start": v(-9.33, -1.1) * mm, "end": v(-9.56, -1.14) * mm});
            skLineSegment(sketch, "E321", {"start": v(-9.56, -1.14) * mm, "end": v(-9.8, -1.17) * mm});
            skLineSegment(sketch, "E322", {"start": v(-9.8, -1.17) * mm, "end": v(-10, -1.27) * mm});
            skLineSegment(sketch, "E323", {"start": v(-10, -1.27) * mm, "end": v(-10.2, -1.37) * mm});
            skLineSegment(sketch, "E324", {"start": v(-10.2, -1.37) * mm, "end": v(-10.4, -1.49) * mm});
            skLineSegment(sketch, "E325", {"start": v(-10.4, -1.49) * mm, "end": v(-10.58, -1.62) * mm});
            skLineSegment(sketch, "E326", {"start": v(-10.58, -1.62) * mm, "end": v(-10.75, -1.77) * mm});
            skLineSegment(sketch, "E327", {"start": v(-10.75, -1.77) * mm, "end": v(-10.9, -1.92) * mm});
            skLineSegment(sketch, "E328", {"start": v(-10.9, -1.92) * mm, "end": v(-11.06, -2.1) * mm});
            skLineSegment(sketch, "E329", {"start": v(-11.06, -2.1) * mm, "end": v(-11.2, -2.28) * mm});
            skLineSegment(sketch, "E330", {"start": v(-11.2, -2.28) * mm, "end": v(-11.32, -2.46) * mm});
            skLineSegment(sketch, "E331", {"start": v(-11.32, -2.46) * mm, "end": v(-11.43, -2.66) * mm});
            skLineSegment(sketch, "E332", {"start": v(-11.43, -2.66) * mm, "end": v(-11.52, -2.87) * mm});
            skLineSegment(sketch, "E333", {"start": v(-11.52, -2.87) * mm, "end": v(-11.54, -2.91) * mm});
            skLineSegment(sketch, "E334", {"start": v(-11.54, -2.91) * mm, "end": v(-11.35, -3.04) * mm});
            skLineSegment(sketch, "E335", {"start": v(-11.35, -3.04) * mm, "end": v(-11.15, -3.15) * mm});
            skLineSegment(sketch, "E336", {"start": v(-11.15, -3.15) * mm, "end": v(-10.95, -3.24) * mm});
            skLineSegment(sketch, "E337", {"start": v(-10.95, -3.24) * mm, "end": v(-10.74, -3.32) * mm});
            skLineSegment(sketch, "E338", {"start": v(-10.74, -3.32) * mm, "end": v(-10.52, -3.39) * mm});
            skLineSegment(sketch, "E339", {"start": v(-10.52, -3.39) * mm, "end": v(-10.3, -3.44) * mm});
            skLineSegment(sketch, "E340", {"start": v(-10.3, -3.44) * mm, "end": v(-10.08, -3.47) * mm});
            skLineSegment(sketch, "E341", {"start": v(-10.08, -3.47) * mm, "end": v(-9.85, -3.49) * mm});
            skLineSegment(sketch, "E342", {"start": v(-9.85, -3.49) * mm, "end": v(-9.63, -3.49) * mm});
            skLineSegment(sketch, "E343", {"start": v(-9.63, -3.49) * mm, "end": v(-9.4, -3.47) * mm});
            skLineSegment(sketch, "E344", {"start": v(-9.4, -3.47) * mm, "end": v(-9.18, -3.43) * mm});
            skLineSegment(sketch, "E345", {"start": v(-9.18, -3.43) * mm, "end": v(-9.13, -3.43) * mm});
            skLineSegment(sketch, "E346", {"start": v(-9.13, -3.43) * mm, "end": v(-8.92, -3.33) * mm});
            skLineSegment(sketch, "E347", {"start": v(-8.92, -3.33) * mm, "end": v(-8.7, -3.23) * mm});
            skLineSegment(sketch, "E348", {"start": v(-8.7, -3.23) * mm, "end": v(-8.49, -3.13) * mm});
            skLineSegment(sketch, "E349", {"start": v(-8.49, -3.13) * mm, "end": v(-8.27, -3.04) * mm});
            skLineSegment(sketch, "E350", {"start": v(-8.27, -3.04) * mm, "end": v(-8.06, -2.94) * mm});
            skLineSegment(sketch, "E351", {"start": v(-8.06, -2.94) * mm, "end": v(-7.84, -2.84) * mm});
            skLineSegment(sketch, "E352", {"start": v(-7.84, -2.84) * mm, "end": v(-7.63, -2.74) * mm});
            skLineSegment(sketch, "E353", {"start": v(-7.63, -2.74) * mm, "end": v(-7.42, -2.64) * mm});
            skLineSegment(sketch, "E354", {"start": v(-7.42, -2.64) * mm, "end": v(-7.2, -2.55) * mm});
            skLineSegment(sketch, "E355", {"start": v(-7.2, -2.55) * mm, "end": v(-6.99, -2.45) * mm});
            skLineSegment(sketch, "E356", {"start": v(-6.99, -2.45) * mm, "end": v(-6.86, -2.64) * mm});
            skLineSegment(sketch, "E357", {"start": v(-6.86, -2.64) * mm, "end": v(-6.74, -2.83) * mm});
            skLineSegment(sketch, "E358", {"start": v(-6.74, -2.83) * mm, "end": v(-6.62, -3.03) * mm});
            skLineSegment(sketch, "E359", {"start": v(-6.62, -3.03) * mm, "end": v(-6.5, -3.22) * mm});
            skLineSegment(sketch, "E360", {"start": v(-6.5, -3.22) * mm, "end": v(-6.37, -3.41) * mm});
            skLineSegment(sketch, "E361", {"start": v(-6.37, -3.41) * mm, "end": v(-6.24, -3.6) * mm});
            skLineSegment(sketch, "E362", {"start": v(-6.24, -3.6) * mm, "end": v(-6.12, -3.8) * mm});
            skLineSegment(sketch, "E363", {"start": v(-6.12, -3.8) * mm, "end": v(-6.08, -3.86) * mm});
            skLineSegment(sketch, "E364", {"start": v(-6.08, -3.86) * mm, "end": v(-6.26, -4.01) * mm});
            skLineSegment(sketch, "E365", {"start": v(-6.26, -4.01) * mm, "end": v(-6.44, -4.17) * mm});
            skLineSegment(sketch, "E366", {"start": v(-6.44, -4.17) * mm, "end": v(-6.61, -4.32) * mm});
            skLineSegment(sketch, "E367", {"start": v(-6.61, -4.32) * mm, "end": v(-6.8, -4.48) * mm});
            skLineSegment(sketch, "E368", {"start": v(-6.8, -4.48) * mm, "end": v(-6.97, -4.63) * mm});
            skLineSegment(sketch, "E369", {"start": v(-6.97, -4.63) * mm, "end": v(-7.15, -4.79) * mm});
            skLineSegment(sketch, "E370", {"start": v(-7.15, -4.79) * mm, "end": v(-7.33, -4.94) * mm});
            skLineSegment(sketch, "E371", {"start": v(-7.33, -4.94) * mm, "end": v(-7.5, -5.1) * mm});
            skLineSegment(sketch, "E372", {"start": v(-7.5, -5.1) * mm, "end": v(-7.68, -5.25) * mm});
            skLineSegment(sketch, "E373", {"start": v(-7.68, -5.25) * mm, "end": v(-7.86, -5.4) * mm});
            skLineSegment(sketch, "E374", {"start": v(-7.86, -5.4) * mm, "end": v(-7.99, -5.6) * mm});
            skLineSegment(sketch, "E375", {"start": v(-7.99, -5.6) * mm, "end": v(-8.1, -5.8) * mm});
            skLineSegment(sketch, "E376", {"start": v(-8.1, -5.8) * mm, "end": v(-8.2, -5.99) * mm});
            skLineSegment(sketch, "E377", {"start": v(-8.2, -5.99) * mm, "end": v(-8.28, -6.2) * mm});
            skLineSegment(sketch, "E378", {"start": v(-8.28, -6.2) * mm, "end": v(-8.35, -6.42) * mm});
            skLineSegment(sketch, "E379", {"start": v(-8.35, -6.42) * mm, "end": v(-8.4, -6.63) * mm});
            skLineSegment(sketch, "E380", {"start": v(-8.4, -6.63) * mm, "end": v(-8.43, -6.86) * mm});
            skLineSegment(sketch, "E381", {"start": v(-8.43, -6.86) * mm, "end": v(-8.45, -7.09) * mm});
            skLineSegment(sketch, "E382", {"start": v(-8.45, -7.09) * mm, "end": v(-8.45, -7.3) * mm});
            skLineSegment(sketch, "E383", {"start": v(-8.45, -7.3) * mm, "end": v(-8.43, -7.54) * mm});
            skLineSegment(sketch, "E384", {"start": v(-8.43, -7.54) * mm, "end": v(-8.4, -7.76) * mm});
            skLineSegment(sketch, "E385", {"start": v(-8.4, -7.76) * mm, "end": v(-8.4, -7.81) * mm});
            skLineSegment(sketch, "E386", {"start": v(-8.4, -7.81) * mm, "end": v(-8.16, -7.81) * mm});
            skLineSegment(sketch, "E387", {"start": v(-8.16, -7.81) * mm, "end": v(-7.94, -7.8) * mm});
            skLineSegment(sketch, "E388", {"start": v(-7.94, -7.8) * mm, "end": v(-7.72, -7.77) * mm});
            skLineSegment(sketch, "E389", {"start": v(-7.72, -7.77) * mm, "end": v(-7.5, -7.72) * mm});
            skLineSegment(sketch, "E390", {"start": v(-7.5, -7.72) * mm, "end": v(-7.28, -7.66) * mm});
            skLineSegment(sketch, "E391", {"start": v(-7.28, -7.66) * mm, "end": v(-7.07, -7.59) * mm});
            skLineSegment(sketch, "E392", {"start": v(-7.07, -7.59) * mm, "end": v(-6.86, -7.5) * mm});
            skLineSegment(sketch, "E393", {"start": v(-6.86, -7.5) * mm, "end": v(-6.66, -7.38) * mm});
            skLineSegment(sketch, "E394", {"start": v(-6.66, -7.38) * mm, "end": v(-6.48, -7.26) * mm});
            skLineSegment(sketch, "E395", {"start": v(-6.48, -7.26) * mm, "end": v(-6.3, -7.12) * mm});
            skLineSegment(sketch, "E396", {"start": v(-6.3, -7.12) * mm, "end": v(-6.12, -6.97) * mm});
            skLineSegment(sketch, "E397", {"start": v(-6.12, -6.97) * mm, "end": v(-6.09, -6.94) * mm});
            skLineSegment(sketch, "E398", {"start": v(-6.09, -6.94) * mm, "end": v(-5.96, -6.74) * mm});
            skLineSegment(sketch, "E399", {"start": v(-5.96, -6.74) * mm, "end": v(-5.83, -6.54) * mm});
            skLineSegment(sketch, "E400", {"start": v(-5.83, -6.54) * mm, "end": v(-5.7, -6.35) * mm});
            skLineSegment(sketch, "E401", {"start": v(-5.7, -6.35) * mm, "end": v(-5.58, -6.15) * mm});
            skLineSegment(sketch, "E402", {"start": v(-5.58, -6.15) * mm, "end": v(-5.45, -5.95) * mm});
            skLineSegment(sketch, "E403", {"start": v(-5.45, -5.95) * mm, "end": v(-5.32, -5.75) * mm});
            skLineSegment(sketch, "E404", {"start": v(-5.32, -5.75) * mm, "end": v(-5.2, -5.55) * mm});
            skLineSegment(sketch, "E405", {"start": v(-5.2, -5.55) * mm, "end": v(-5.07, -5.35) * mm});
            skLineSegment(sketch, "E406", {"start": v(-5.07, -5.35) * mm, "end": v(-4.94, -5.16) * mm});
            skLineSegment(sketch, "E407", {"start": v(-4.94, -5.16) * mm, "end": v(-4.81, -4.96) * mm});
            skLineSegment(sketch, "E408", {"start": v(-4.81, -4.96) * mm, "end": v(-4.6, -5.05) * mm});
            skLineSegment(sketch, "E409", {"start": v(-4.6, -5.05) * mm, "end": v(-4.4, -5.15) * mm});
            skLineSegment(sketch, "E410", {"start": v(-4.4, -5.15) * mm, "end": v(-4.19, -5.24) * mm});
            skLineSegment(sketch, "E411", {"start": v(-4.19, -5.24) * mm, "end": v(-3.98, -5.34) * mm});
            skLineSegment(sketch, "E412", {"start": v(-3.98, -5.34) * mm, "end": v(-3.77, -5.43) * mm});
            skLineSegment(sketch, "E413", {"start": v(-3.77, -5.43) * mm, "end": v(-3.56, -5.53) * mm});
            skLineSegment(sketch, "E414", {"start": v(-3.56, -5.53) * mm, "end": v(-3.35, -5.63) * mm});
            skLineSegment(sketch, "E415", {"start": v(-3.35, -5.63) * mm, "end": v(-3.29, -5.66) * mm});
            skLineSegment(sketch, "E416", {"start": v(-3.29, -5.66) * mm, "end": v(-3.35, -5.88) * mm});
            skLineSegment(sketch, "E417", {"start": v(-3.35, -5.88) * mm, "end": v(-3.42, -6.1) * mm});
            skLineSegment(sketch, "E418", {"start": v(-3.42, -6.1) * mm, "end": v(-3.49, -6.33) * mm});
            skLineSegment(sketch, "E419", {"start": v(-3.49, -6.33) * mm, "end": v(-3.55, -6.56) * mm});
            skLineSegment(sketch, "E420", {"start": v(-3.55, -6.56) * mm, "end": v(-3.62, -6.79) * mm});
            skLineSegment(sketch, "E421", {"start": v(-3.62, -6.79) * mm, "end": v(-3.68, -7.01) * mm});
            skLineSegment(sketch, "E422", {"start": v(-3.68, -7.01) * mm, "end": v(-3.75, -7.24) * mm});
            skLineSegment(sketch, "E423", {"start": v(-3.75, -7.24) * mm, "end": v(-3.82, -7.46) * mm});
            skLineSegment(sketch, "E424", {"start": v(-3.82, -7.46) * mm, "end": v(-3.88, -7.69) * mm});
            skLineSegment(sketch, "E425", {"start": v(-3.88, -7.69) * mm, "end": v(-3.95, -7.92) * mm});
            skLineSegment(sketch, "E426", {"start": v(-3.95, -7.92) * mm, "end": v(-3.95, -8.15) * mm});
            skLineSegment(sketch, "E427", {"start": v(-3.95, -8.15) * mm, "end": v(-3.94, -8.37) * mm});
            skLineSegment(sketch, "E428", {"start": v(-3.94, -8.37) * mm, "end": v(-3.92, -8.6) * mm});
            skLineSegment(sketch, "E429", {"start": v(-3.92, -8.6) * mm, "end": v(-3.87, -8.82) * mm});
            skLineSegment(sketch, "E430", {"start": v(-3.87, -8.82) * mm, "end": v(-3.8, -9.04) * mm});
            skLineSegment(sketch, "E431", {"start": v(-3.8, -9.04) * mm, "end": v(-3.74, -9.24) * mm});
            skLineSegment(sketch, "E432", {"start": v(-3.74, -9.24) * mm, "end": v(-3.64, -9.45) * mm});
            skLineSegment(sketch, "E433", {"start": v(-3.64, -9.45) * mm, "end": v(-3.53, -9.65) * mm});
            skLineSegment(sketch, "E434", {"start": v(-3.53, -9.65) * mm, "end": v(-3.42, -9.84) * mm});
            skLineSegment(sketch, "E435", {"start": v(-3.42, -9.84) * mm, "end": v(-3.28, -10.02) * mm});
            skLineSegment(sketch, "E436", {"start": v(-3.28, -10.02) * mm, "end": v(-3.13, -10.2) * mm});
            skLineSegment(sketch, "E437", {"start": v(-3.13, -10.2) * mm, "end": v(-3.1, -10.23) * mm});
            skLineSegment(sketch, "E438", {"start": v(-3.1, -10.23) * mm, "end": v(-2.9, -10.1) * mm});
            skLineSegment(sketch, "E439", {"start": v(-2.9, -10.1) * mm, "end": v(-2.72, -9.97) * mm});
            skLineSegment(sketch, "E440", {"start": v(-2.72, -9.97) * mm, "end": v(-2.55, -9.83) * mm});
            skLineSegment(sketch, "E441", {"start": v(-2.55, -9.83) * mm, "end": v(-2.39, -9.67) * mm});
            skLineSegment(sketch, "E442", {"start": v(-2.39, -9.67) * mm, "end": v(-2.24, -9.5) * mm});
            skLineSegment(sketch, "E443", {"start": v(-2.24, -9.5) * mm, "end": v(-2.1, -9.33) * mm});
            skLineSegment(sketch, "E444", {"start": v(-2.1, -9.33) * mm, "end": v(-1.98, -9.13) * mm});
            skLineSegment(sketch, "E445", {"start": v(-1.98, -9.13) * mm, "end": v(-1.87, -8.93) * mm});
            skLineSegment(sketch, "E446", {"start": v(-1.87, -8.93) * mm, "end": v(-1.78, -8.73) * mm});
            skLineSegment(sketch, "E447", {"start": v(-1.78, -8.73) * mm, "end": v(-1.7, -8.52) * mm});
            skLineSegment(sketch, "E448", {"start": v(-1.7, -8.52) * mm, "end": v(-1.64, -8.3) * mm});
            skLineSegment(sketch, "E449", {"start": v(-1.64, -8.3) * mm, "end": v(-1.63, -8.25) * mm});
            skLineSegment(sketch, "E450", {"start": v(-1.63, -8.25) * mm, "end": v(-1.63, -8.01) * mm});
            skLineSegment(sketch, "E451", {"start": v(-1.63, -8.01) * mm, "end": v(-1.63, -7.78) * mm});
            skLineSegment(sketch, "E452", {"start": v(-1.63, -7.78) * mm, "end": v(-1.63, -7.54) * mm});
            skLineSegment(sketch, "E453", {"start": v(-1.63, -7.54) * mm, "end": v(-1.63, -7.3) * mm});
            skLineSegment(sketch, "E454", {"start": v(-1.63, -7.3) * mm, "end": v(-1.63, -7.07) * mm});
            skLineSegment(sketch, "E455", {"start": v(-1.63, -7.07) * mm, "end": v(-1.63, -6.84) * mm});
            skLineSegment(sketch, "E456", {"start": v(-1.63, -6.84) * mm, "end": v(-1.63, -6.6) * mm});
            skLineSegment(sketch, "E457", {"start": v(-1.63, -6.6) * mm, "end": v(-1.63, -6.37) * mm});
            skLineSegment(sketch, "E458", {"start": v(-1.63, -6.37) * mm, "end": v(-1.63, -6.13) * mm});
            skLineSegment(sketch, "E459", {"start": v(-1.63, -6.13) * mm, "end": v(-1.63, -5.9) * mm});
            skLineSegment(sketch, "E460", {"start": v(-1.63, -5.9) * mm, "end": v(-1.4, -5.86) * mm});
            skLineSegment(sketch, "E461", {"start": v(-1.4, -5.86) * mm, "end": v(-1.17, -5.83) * mm});
            skLineSegment(sketch, "E462", {"start": v(-1.17, -5.83) * mm, "end": v(-0.95, -5.8) * mm});
            skLineSegment(sketch, "E463", {"start": v(-0.95, -5.8) * mm, "end": v(-0.72, -5.76) * mm});
            skLineSegment(sketch, "E464", {"start": v(-0.72, -5.76) * mm, "end": v(-0.5, -5.73) * mm});
            skLineSegment(sketch, "E465", {"start": v(-0.5, -5.73) * mm, "end": v(-0.26, -5.7) * mm});
            skLineSegment(sketch, "E466", {"start": v(-0.26, -5.7) * mm, "end": v(-0.04, -5.67) * mm});
            skLineSegment(sketch, "E467", {"start": v(-0.04, -5.67) * mm, "end": v(0.03, -5.66) * mm});
            skLineSegment(sketch, "E468", {"start": v(0.03, -5.66) * mm, "end": v(0.1, -5.88) * mm});
            skLineSegment(sketch, "E469", {"start": v(0.1, -5.88) * mm, "end": v(0.17, -6.1) * mm});
            skLineSegment(sketch, "E470", {"start": v(0.17, -6.1) * mm, "end": v(0.23, -6.33) * mm});
            skLineSegment(sketch, "E471", {"start": v(0.23, -6.33) * mm, "end": v(0.3, -6.56) * mm});
            skLineSegment(sketch, "E472", {"start": v(0.3, -6.56) * mm, "end": v(0.37, -6.79) * mm});
            skLineSegment(sketch, "E473", {"start": v(0.37, -6.79) * mm, "end": v(0.43, -7.01) * mm});
            skLineSegment(sketch, "E474", {"start": v(0.43, -7.01) * mm, "end": v(0.5, -7.24) * mm});
            skLineSegment(sketch, "E475", {"start": v(0.5, -7.24) * mm, "end": v(0.57, -7.46) * mm});
            skLineSegment(sketch, "E476", {"start": v(0.57, -7.46) * mm, "end": v(0.63, -7.69) * mm});
            skLineSegment(sketch, "E477", {"start": v(0.63, -7.69) * mm, "end": v(0.7, -7.92) * mm});
            skLineSegment(sketch, "E478", {"start": v(0.7, -7.92) * mm, "end": v(0.82, -8.11) * mm});
            skLineSegment(sketch, "E479", {"start": v(0.82, -8.11) * mm, "end": v(0.95, -8.3) * mm});
            skLineSegment(sketch, "E480", {"start": v(0.95, -8.3) * mm, "end": v(1.1, -8.46) * mm});
            skLineSegment(sketch, "E481", {"start": v(1.1, -8.46) * mm, "end": v(1.25, -8.63) * mm});
            skLineSegment(sketch, "E482", {"start": v(1.25, -8.63) * mm, "end": v(1.42, -8.78) * mm});
            skLineSegment(sketch, "E483", {"start": v(1.42, -8.78) * mm, "end": v(1.6, -8.91) * mm});
            skLineSegment(sketch, "E484", {"start": v(1.6, -8.91) * mm, "end": v(1.79, -9.04) * mm});
            skLineSegment(sketch, "E485", {"start": v(1.79, -9.04) * mm, "end": v(1.99, -9.15) * mm});
            skLineSegment(sketch, "E486", {"start": v(1.99, -9.15) * mm, "end": v(2.19, -9.24) * mm});
            skLineSegment(sketch, "E487", {"start": v(2.19, -9.24) * mm, "end": v(2.4, -9.32) * mm});
            skLineSegment(sketch, "E488", {"start": v(2.4, -9.32) * mm, "end": v(2.62, -9.39) * mm});
            skLineSegment(sketch, "E489", {"start": v(2.62, -9.39) * mm, "end": v(2.67, -9.4) * mm});
            skLineSegment(sketch, "E490", {"start": v(2.67, -9.4) * mm, "end": v(2.76, -9.2) * mm});
            skLineSegment(sketch, "E491", {"start": v(2.76, -9.2) * mm, "end": v(2.85, -8.98) * mm});
            skLineSegment(sketch, "E492", {"start": v(2.85, -8.98) * mm, "end": v(2.91, -8.77) * mm});
            skLineSegment(sketch, "E493", {"start": v(2.91, -8.77) * mm, "end": v(2.96, -8.55) * mm});
            skLineSegment(sketch, "E494", {"start": v(2.96, -8.55) * mm, "end": v(3, -8.32) * mm});
            skLineSegment(sketch, "E495", {"start": v(3, -8.32) * mm, "end": v(3.01, -8.1) * mm});
            skLineSegment(sketch, "E496", {"start": v(3.01, -8.1) * mm, "end": v(3.01, -7.87) * mm});
            skLineSegment(sketch, "E497", {"start": v(3.01, -7.87) * mm, "end": v(3, -7.65) * mm});
            skLineSegment(sketch, "E498", {"start": v(3, -7.65) * mm, "end": v(2.97, -7.43) * mm});
            skLineSegment(sketch, "E499", {"start": v(2.97, -7.43) * mm, "end": v(2.92, -7.2) * mm});
            skLineSegment(sketch, "E500", {"start": v(2.92, -7.2) * mm, "end": v(2.85, -6.99) * mm});
            skLineSegment(sketch, "E501", {"start": v(2.85, -6.99) * mm, "end": v(2.83, -6.94) * mm});
            skLineSegment(sketch, "E502", {"start": v(2.83, -6.94) * mm, "end": v(2.7, -6.74) * mm});
            skLineSegment(sketch, "E503", {"start": v(2.7, -6.74) * mm, "end": v(2.58, -6.54) * mm});
            skLineSegment(sketch, "E504", {"start": v(2.58, -6.54) * mm, "end": v(2.45, -6.35) * mm});
            skLineSegment(sketch, "E505", {"start": v(2.45, -6.35) * mm, "end": v(2.32, -6.15) * mm});
            skLineSegment(sketch, "E506", {"start": v(2.32, -6.15) * mm, "end": v(2.2, -5.95) * mm});
            skLineSegment(sketch, "E507", {"start": v(2.2, -5.95) * mm, "end": v(2.07, -5.75) * mm});
            skLineSegment(sketch, "E508", {"start": v(2.07, -5.75) * mm, "end": v(1.94, -5.55) * mm});
            skLineSegment(sketch, "E509", {"start": v(1.94, -5.55) * mm, "end": v(1.82, -5.35) * mm});
            skLineSegment(sketch, "E510", {"start": v(1.82, -5.35) * mm, "end": v(1.69, -5.16) * mm});
            skLineSegment(sketch, "E511", {"start": v(1.69, -5.16) * mm, "end": v(1.56, -4.96) * mm});
            skLineSegment(sketch, "E512", {"start": v(1.56, -4.96) * mm, "end": v(1.73, -4.8) * mm});
            skLineSegment(sketch, "E513", {"start": v(1.73, -4.8) * mm, "end": v(1.9, -4.66) * mm});
            skLineSegment(sketch, "E514", {"start": v(1.9, -4.66) * mm, "end": v(2.08, -4.5) * mm});
            skLineSegment(sketch, "E515", {"start": v(2.08, -4.5) * mm, "end": v(2.25, -4.36) * mm});
            skLineSegment(sketch, "E516", {"start": v(2.25, -4.36) * mm, "end": v(2.43, -4.2) * mm});
            skLineSegment(sketch, "E517", {"start": v(2.43, -4.2) * mm, "end": v(2.6, -4.06) * mm});
            skLineSegment(sketch, "E518", {"start": v(2.6, -4.06) * mm, "end": v(2.77, -3.9) * mm});
            skLineSegment(sketch, "E519", {"start": v(2.77, -3.9) * mm, "end": v(2.83, -3.86) * mm});
            skLineSegment(sketch, "E520", {"start": v(2.83, -3.86) * mm, "end": v(3, -4.01) * mm});
            skLineSegment(sketch, "E521", {"start": v(3, -4.01) * mm, "end": v(3.18, -4.17) * mm});
            skLineSegment(sketch, "E522", {"start": v(3.18, -4.17) * mm, "end": v(3.36, -4.32) * mm});
            skLineSegment(sketch, "E523", {"start": v(3.36, -4.32) * mm, "end": v(3.54, -4.48) * mm});
            skLineSegment(sketch, "E524", {"start": v(3.54, -4.48) * mm, "end": v(3.72, -4.63) * mm});
            skLineSegment(sketch, "E525", {"start": v(3.72, -4.63) * mm, "end": v(3.9, -4.79) * mm});
            skLineSegment(sketch, "E526", {"start": v(3.9, -4.79) * mm, "end": v(4.07, -4.94) * mm});
            skLineSegment(sketch, "E527", {"start": v(4.07, -4.94) * mm, "end": v(4.25, -5.1) * mm});
            skLineSegment(sketch, "E528", {"start": v(4.25, -5.1) * mm, "end": v(4.43, -5.25) * mm});
            skLineSegment(sketch, "E529", {"start": v(4.43, -5.25) * mm, "end": v(4.6, -5.4) * mm});
            skLineSegment(sketch, "E530", {"start": v(4.6, -5.4) * mm, "end": v(4.82, -5.5) * mm});
            skLineSegment(sketch, "E531", {"start": v(4.82, -5.5) * mm, "end": v(5.03, -5.58) * mm});
            skLineSegment(sketch, "E532", {"start": v(5.03, -5.58) * mm, "end": v(5.24, -5.65) * mm});
            skLineSegment(sketch, "E533", {"start": v(5.24, -5.65) * mm, "end": v(5.46, -5.7) * mm});
            skLineSegment(sketch, "E534", {"start": v(5.46, -5.7) * mm, "end": v(5.69, -5.74) * mm});
            skLineSegment(sketch, "E535", {"start": v(5.69, -5.74) * mm, "end": v(5.9, -5.76) * mm});
            skLineSegment(sketch, "E536", {"start": v(5.9, -5.76) * mm, "end": v(6.13, -5.76) * mm});
            skLineSegment(sketch, "E537", {"start": v(6.13, -5.76) * mm, "end": v(6.36, -5.74) * mm});
            skLineSegment(sketch, "E538", {"start": v(6.36, -5.74) * mm, "end": v(6.58, -5.72) * mm});
            skLineSegment(sketch, "E539", {"start": v(6.58, -5.72) * mm, "end": v(6.8, -5.67) * mm});
            skLineSegment(sketch, "E540", {"start": v(6.8, -5.67) * mm, "end": v(7.02, -5.6) * mm});
            skLineSegment(sketch, "E541", {"start": v(7.02, -5.6) * mm, "end": v(7.07, -5.59) * mm});
            skLineSegment(sketch, "E542", {"start": v(7.07, -5.59) * mm, "end": v(7.04, -5.36) * mm});
            skLineSegment(sketch, "E543", {"start": v(7.04, -5.36) * mm, "end": v(7, -5.14) * mm});
            skLineSegment(sketch, "E544", {"start": v(7, -5.14) * mm, "end": v(6.93, -4.93) * mm});
            skLineSegment(sketch, "E545", {"start": v(6.93, -4.93) * mm, "end": v(6.85, -4.71) * mm});
            skLineSegment(sketch, "E546", {"start": v(6.85, -4.71) * mm, "end": v(6.76, -4.5) * mm});
            skLineSegment(sketch, "E547", {"start": v(6.76, -4.5) * mm, "end": v(6.66, -4.3) * mm});
            skLineSegment(sketch, "E548", {"start": v(6.66, -4.3) * mm, "end": v(6.53, -4.12) * mm});
            skLineSegment(sketch, "E549", {"start": v(6.53, -4.12) * mm, "end": v(6.4, -3.93) * mm});
            skLineSegment(sketch, "E550", {"start": v(6.4, -3.93) * mm, "end": v(6.25, -3.77) * mm});
            skLineSegment(sketch, "E551", {"start": v(6.25, -3.77) * mm, "end": v(6.1, -3.6) * mm});
            skLineSegment(sketch, "E552", {"start": v(6.1, -3.6) * mm, "end": v(5.92, -3.46) * mm});
            skLineSegment(sketch, "E553", {"start": v(5.92, -3.46) * mm, "end": v(5.88, -3.43) * mm});
            skLineSegment(sketch, "E554", {"start": v(5.88, -3.43) * mm, "end": v(5.66, -3.33) * mm});
            skLineSegment(sketch, "E555", {"start": v(5.66, -3.33) * mm, "end": v(5.45, -3.23) * mm});
            skLineSegment(sketch, "E556", {"start": v(5.45, -3.23) * mm, "end": v(5.24, -3.13) * mm});
            skLineSegment(sketch, "E557", {"start": v(5.24, -3.13) * mm, "end": v(5.02, -3.04) * mm});
            skLineSegment(sketch, "E558", {"start": v(5.02, -3.04) * mm, "end": v(4.8, -2.94) * mm});
            skLineSegment(sketch, "E559", {"start": v(4.8, -2.94) * mm, "end": v(4.6, -2.84) * mm});
            skLineSegment(sketch, "E560", {"start": v(4.6, -2.84) * mm, "end": v(4.38, -2.74) * mm});
            skLineSegment(sketch, "E561", {"start": v(4.38, -2.74) * mm, "end": v(4.16, -2.64) * mm});
            skLineSegment(sketch, "E562", {"start": v(4.16, -2.64) * mm, "end": v(3.95, -2.55) * mm});
            skLineSegment(sketch, "E563", {"start": v(3.95, -2.55) * mm, "end": v(3.74, -2.45) * mm});
            skLineSegment(sketch, "E564", {"start": v(3.74, -2.45) * mm, "end": v(3.8, -2.23) * mm});
            skLineSegment(sketch, "E565", {"start": v(3.8, -2.23) * mm, "end": v(3.86, -2) * mm});
            skLineSegment(sketch, "E566", {"start": v(3.86, -2) * mm, "end": v(3.93, -1.79) * mm});
            skLineSegment(sketch, "E567", {"start": v(3.93, -1.79) * mm, "end": v(4, -1.57) * mm});
            skLineSegment(sketch, "E568", {"start": v(4, -1.57) * mm, "end": v(4.06, -1.35) * mm});
            skLineSegment(sketch, "E569", {"start": v(4.06, -1.35) * mm, "end": v(4.12, -1.13) * mm});
            skLineSegment(sketch, "E570", {"start": v(4.12, -1.13) * mm, "end": v(4.19, -0.9) * mm});
            skLineSegment(sketch, "E571", {"start": v(4.19, -0.9) * mm, "end": v(4.2, -0.84) * mm});
            skLineSegment(sketch, "E572", {"start": v(-2.74, -1) * mm, "end": v(-0.5, -1) * mm});
            skCircle(sketch, "E573", {"center": v(-1.63, 0) * mm, "radius": 1.5 * mm});
            skPoint(sketch, "E574", {"position": v(-1.63, -1) * mm});
            skSolve(sketch);
        }
        {
            var Q0;
            Q0=makeQuery(id+"F0.imprint","IMPRINT",FACE,{"disambiguationData":[TD([[makeQuery(id+"F0.imprint","IMPRINT",EDGE,{"derivedFrom":sQuery(id+"F0.wireOp",EDGE,"E0")}),1.0]])]});
            var Q1;
            {var subQ0=sQuery(id+"F0.wireOp",EDGE,"E572");Q1=makeQuery(id+"F0.imprint","IMPRINT",FACE,{"disambiguationData":[TD([[makeQuery(id+"F0.imprint","IMPRINT",EDGE,{"derivedFrom":subQ0}),-1.0]])]});}
            extrude(context, id + "F1", {"entities" : qUnion([Q0, Q1]), "depth" : 5 * mm});
        }
    });
